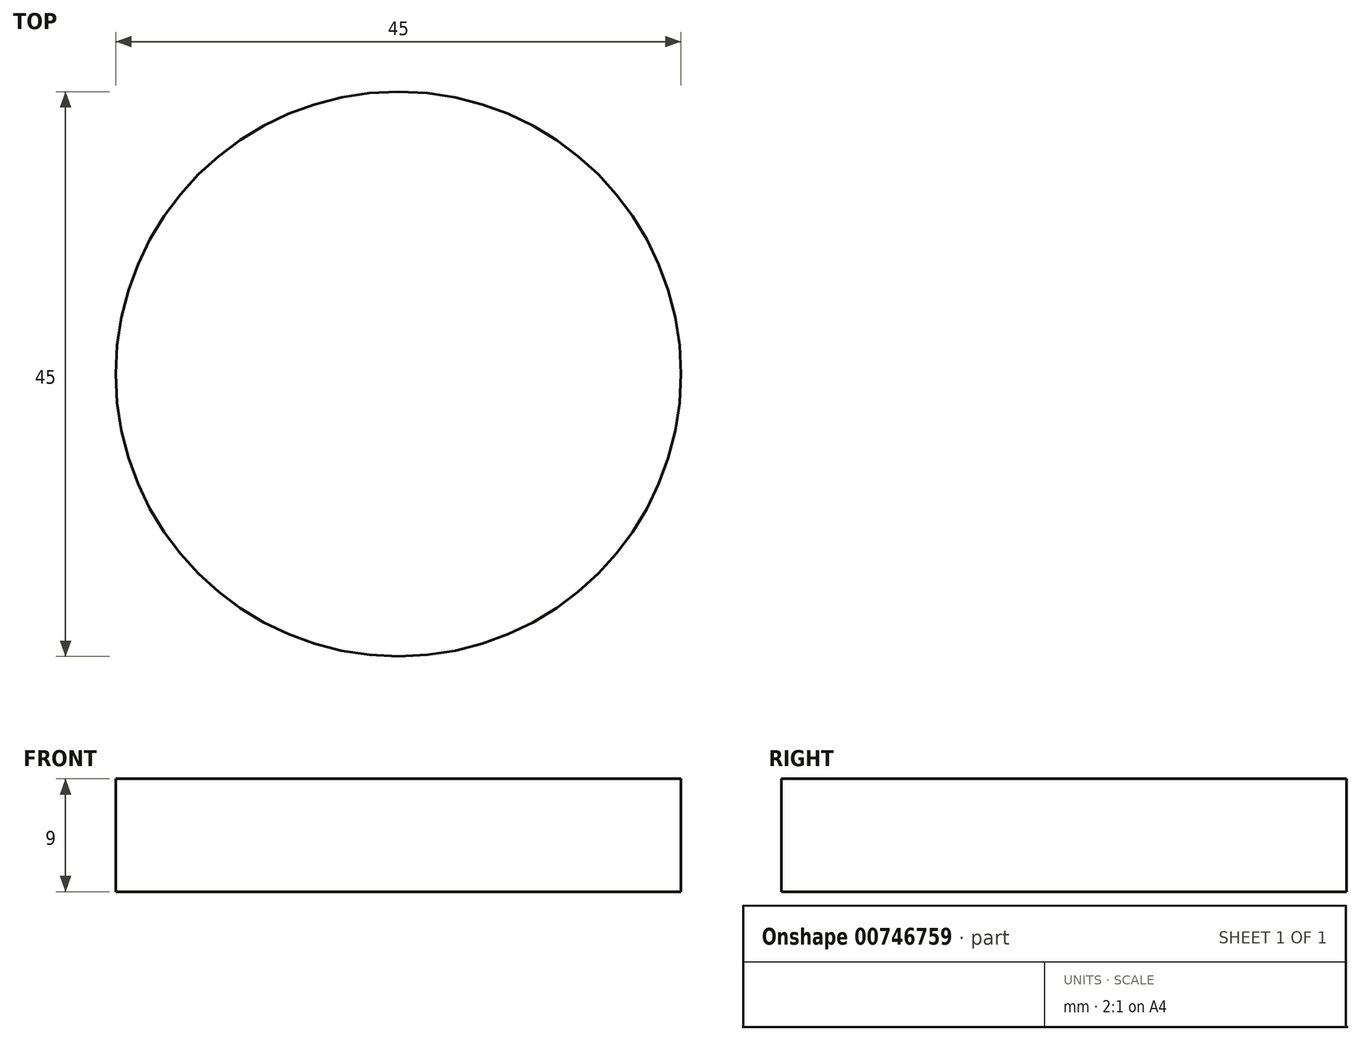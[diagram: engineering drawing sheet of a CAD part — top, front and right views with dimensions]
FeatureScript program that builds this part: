
annotation { "Feature Type Name" : "Feature", "Feature Type Description" : "" }
export const myFeature = defineFeature(function(context is Context, id is Id, definition is map)
    precondition{}
    {
        {
            var Q0;
            Q0=qCreatedBy(makeId("Top.planeOp"),FACE);
            var sketch = newSketch(context, id + "F0", { "sketchPlane" : qUnion([Q0])});
            skCircle(sketch, "E0", {"center": v(0, 0) * mm, "radius": 22.5 * mm});
            skSolve(sketch);
        }
        {
            var Q0;
            Q0=makeQuery(id+"F0.imprint","IMPRINT",FACE,{"disambiguationData":[TD([[makeQuery(id+"F0.imprint","IMPRINT",EDGE,{"derivedFrom":sQuery(id+"F0.wireOp",EDGE,"E0")}),1.0]])]});
            extrude(context, id + "F1", {"entities" : qUnion([Q0]), "depth" : 9 * mm, "offsetDistance" : 25 * mm});
        }
    });
